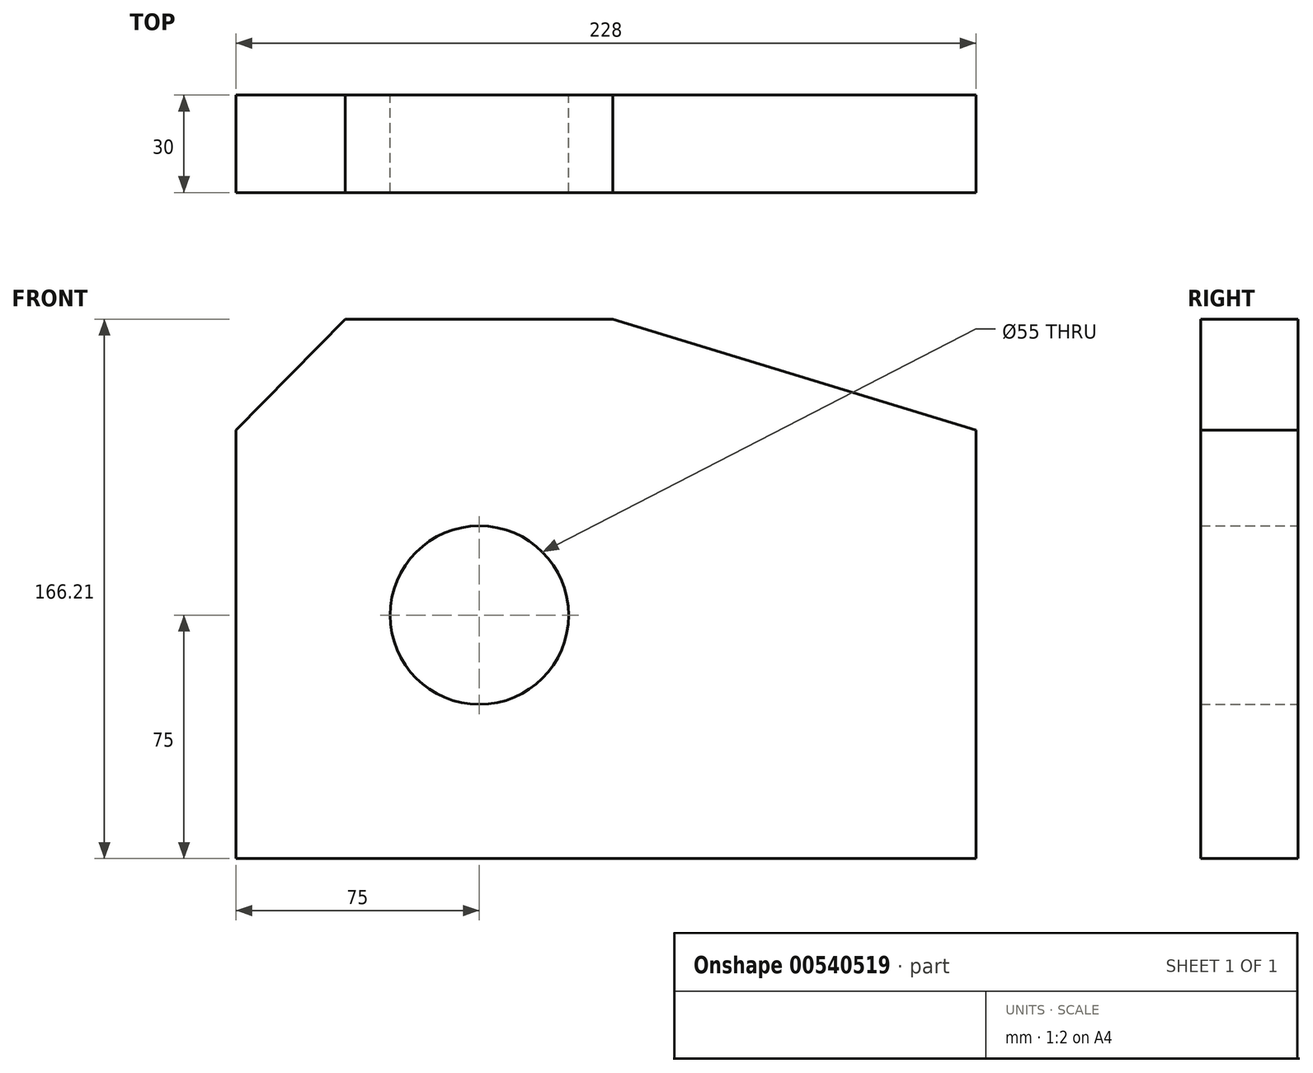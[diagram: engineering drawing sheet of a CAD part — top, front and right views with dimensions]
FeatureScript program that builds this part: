
annotation { "Feature Type Name" : "Feature", "Feature Type Description" : "" }
export const myFeature = defineFeature(function(context is Context, id is Id, definition is map)
    precondition{}
    {
        {
            var Q0;
            Q0=qCreatedBy(makeId("Front.planeOp"),FACE);
            var sketch = newSketch(context, id + "F0", { "sketchPlane" : qUnion([Q0])});
            skLineSegment(sketch, "E0", {"start": v(0, 0) * mm, "end": v(-228, 0) * mm});
            skLineSegment(sketch, "E1", {"start": v(-228, 0) * mm, "end": v(-228, 132) * mm});
            skLineSegment(sketch, "E2", {"start": v(-228, 132) * mm, "end": v(-194.33, 166.2) * mm});
            skLineSegment(sketch, "E3", {"start": v(-194.33, 166.2) * mm, "end": v(-111.89, 166.2) * mm});
            skLineSegment(sketch, "E4", {"start": v(-111.89, 166.2) * mm, "end": v(0, 132) * mm});
            skLineSegment(sketch, "E5", {"start": v(0, 132) * mm, "end": v(0, 0) * mm});
            skCircle(sketch, "E6", {"center": v(-153, 75) * mm, "radius": 27.5 * mm});
            skLineSegment(sketch, "E7", {"start": v(-153, 75) * mm, "end": v(-153, 0) * mm, "construction": true});
            skSolve(sketch);
        }
        {
            var Q0;
            Q0 = qSketchRegion(id + "F0", true);
            extrude(context, id + "F1", {"entities" : qUnion([Q0]), "depth" : 30 * mm, "offsetDistance" : 25 * mm});
        }
    });
